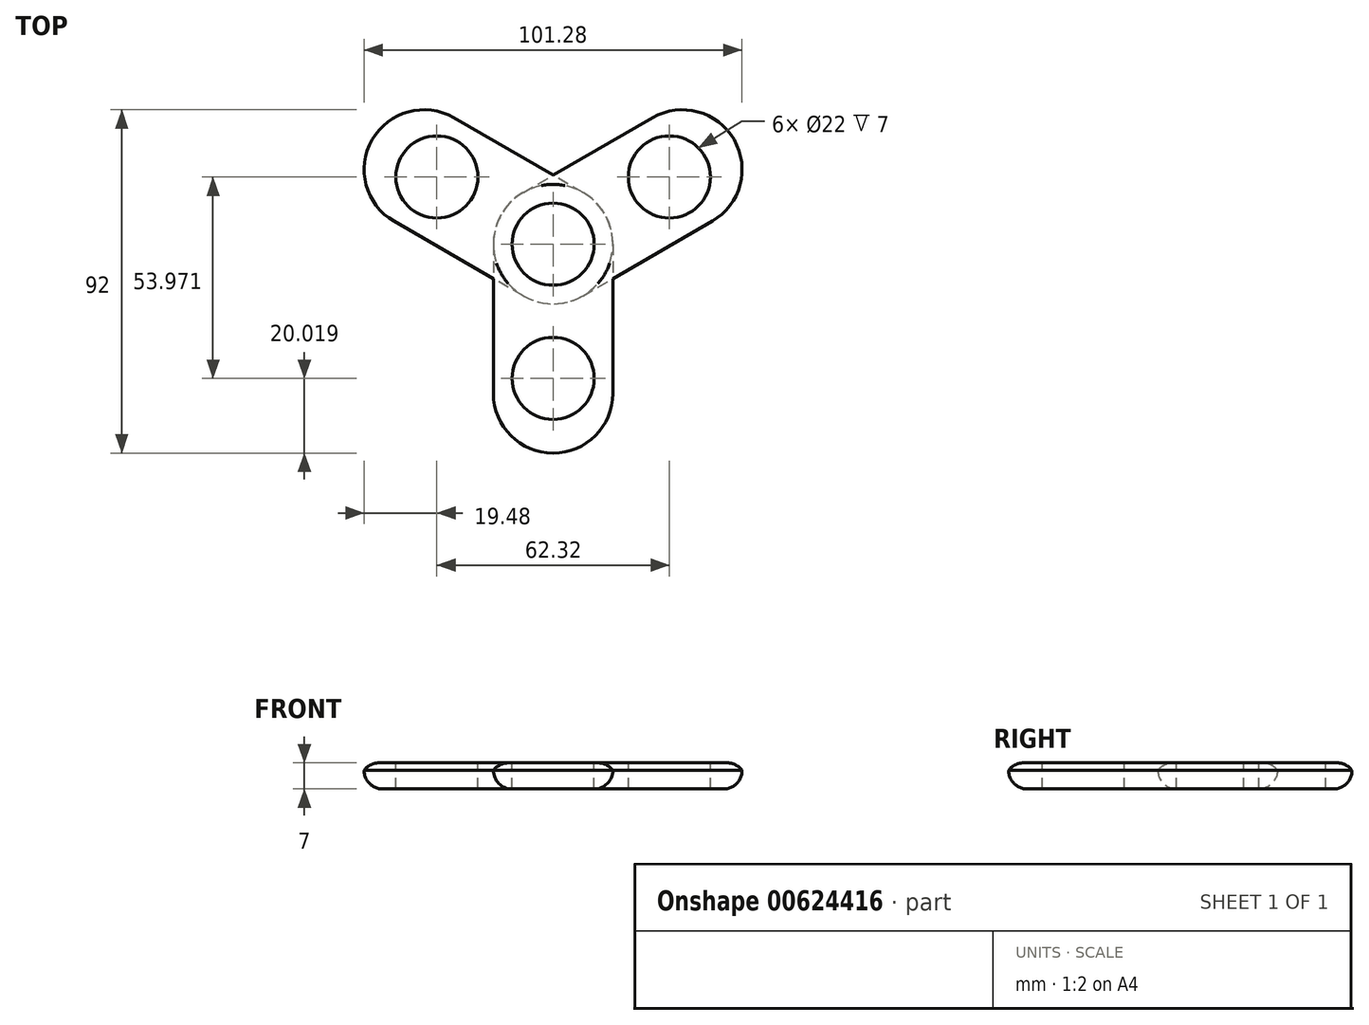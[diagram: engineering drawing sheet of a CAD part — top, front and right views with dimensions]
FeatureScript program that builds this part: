
annotation { "Feature Type Name" : "Feature", "Feature Type Description" : "" }
export const myFeature = defineFeature(function(context is Context, id is Id, definition is map)
    precondition{}
    {
        {
            var Q0;
            Q0=qCreatedBy(makeId("Top.planeOp"),FACE);
            var sketch = newSketch(context, id + "F0", { "sketchPlane" : qUnion([Q0])});
            skCircle(sketch, "E0", {"center": v(0, 0) * mm, "radius": 16 * mm});
            skCircle(sketch, "E1", {"center": v(0, -40) * mm, "radius": 16 * mm});
            skLineSegment(sketch, "E2", {"start": v(16, 0) * mm, "end": v(16, -40) * mm});
            skLineSegment(sketch, "E3", {"start": v(-16, 0) * mm, "end": v(-16, -40) * mm});
            skSolve(sketch);
        }
        {
            var Q0;
            Q0 = qSketchRegion(id + "F0", true);
            extrude(context, id + "F1", {"entities" : qUnion([Q0]), "depth" : 7 * mm, "offsetDistance" : 25 * mm});
        }
        {
            var Q0;
            Q0=makeQuery(id+"F1.opExtrude","CAP_FACE",FACE,{"disambiguationData":[OSD([sQuery(id+"F0.wireOp",EDGE,"E0"),sQuery(id+"F0.wireOp",EDGE,"E1"),sQuery(id+"F0.wireOp",EDGE,"E2"),sQuery(id+"F0.wireOp",EDGE,"E3")])],"isStart":false});
            var sketch = newSketch(context, id + "F2", { "sketchPlane" : qUnion([Q0])});
            skCircle(sketch, "E4", {"center": v(0, 0) * mm, "radius": 11 * mm});
            skCircle(sketch, "E5", {"center": v(0, -35.98) * mm, "radius": 11 * mm});
            skSolve(sketch);
        }
        {
            var Q0;
            Q0 = qSketchRegion(id + "F2", true);
            extrude(context, id + "F3", {"entities" : qUnion([Q0]), "operationType" : NewBodyOperationType.REMOVE, "oppositeDirection" : true, "depth" : 7 * mm, "offsetDistance" : 25 * mm});
        }
        {
            var Q0;
            Q0=qCreatedBy(makeId("Front.planeOp"),FACE);
            var sketch = newSketch(context, id + "F4", { "sketchPlane" : qUnion([Q0])});
            skLineSegment(sketch, "E6", {"start": v(0, 0) * mm, "end": v(0, 55.38) * mm});
            skSolve(sketch);
        }
        {
            var Q0;
            Q0=makeQuery(id+"F1.opExtrude","SWEPT_BODY",BODY,{"disambiguationData":[OSD([sQuery(id+"F0.wireOp",EDGE,"E0"),sQuery(id+"F0.wireOp",EDGE,"E1"),sQuery(id+"F0.wireOp",EDGE,"E2"),sQuery(id+"F0.wireOp",EDGE,"E3")])]});
            var Q1;
            Q1=sQuery(id+"F4.wireOp",EDGE,"E6");
            circularPattern(context, id + "F5", {"entities" : qUnion([Q0]), "axis" : qUnion([Q1]), "angle" : 360 * degree, "instanceCount" : 3, "equalSpace" : true});
        }
        {
            var Q0;
            Q0=makeQuery(id+"F5.opPattern","COPY",EDGE,{"derivedFrom":makeQuery(id+"F1.opExtrude","CAP_EDGE",EDGE,{"disambiguationData":[OSD([sQuery(id+"F0.wireOp",EDGE,"E3")])],"isStart":true}),"instanceName":"2"});
            var Q1;
            Q1=makeQuery(id+"F5.opPattern","COPY",EDGE,{"derivedFrom":makeQuery(id+"F1.opExtrude","CAP_EDGE",EDGE,{"disambiguationData":[OSD([sQuery(id+"F0.wireOp",EDGE,"E2")])],"isStart":true}),"instanceName":"1"});
            var Q2;
            Q2=makeQuery(id+"F1.opExtrude","CAP_EDGE",EDGE,{"disambiguationData":[OSD([sQuery(id+"F0.wireOp",EDGE,"E2")])],"isStart":true});
            fillet(context, id + "F6", {"entities" : qUnion([Q0, Q1, Q2]), "radius" : 5 * mm, "tangentPropagation" : true, "allowEdgeOverflow" : false});
        }
        {
            var Q0;
            Q0=makeQuery(id+"F5.opPattern","COPY",EDGE,{"derivedFrom":makeQuery(id+"F1.opExtrude","CAP_EDGE",EDGE,{"disambiguationData":[OSD([sQuery(id+"F0.wireOp",EDGE,"E3")])],"isStart":false}),"instanceName":"1"});
            var Q1;
            Q1=makeQuery(id+"F1.opExtrude","CAP_EDGE",EDGE,{"disambiguationData":[OSD([sQuery(id+"F0.wireOp",EDGE,"E2")])],"isStart":false});
            var Q2;
            Q2=makeQuery(id+"F5.opPattern","COPY",EDGE,{"derivedFrom":makeQuery(id+"F1.opExtrude","CAP_EDGE",EDGE,{"disambiguationData":[OSD([sQuery(id+"F0.wireOp",EDGE,"E2")])],"isStart":false}),"instanceName":"2"});
            fillet(context, id + "F7", {"entities" : qUnion([Q0, Q1, Q2]), "radius" : 5 * mm, "tangentPropagation" : true, "allowEdgeOverflow" : false});
        }
    });
